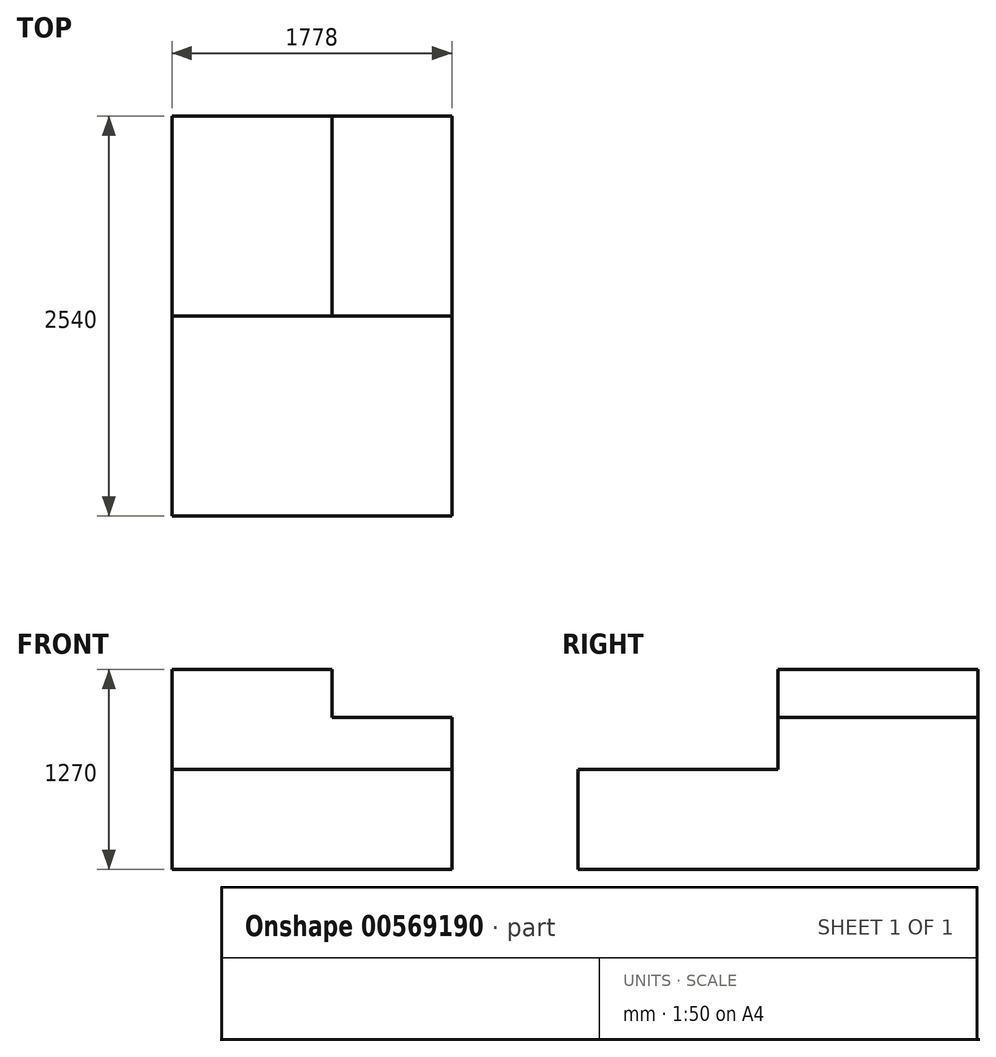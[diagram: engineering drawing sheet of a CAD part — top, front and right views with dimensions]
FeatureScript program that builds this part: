
annotation { "Feature Type Name" : "Feature", "Feature Type Description" : "" }
export const myFeature = defineFeature(function(context is Context, id is Id, definition is map)
    precondition{}
    {
        {
            var Q0;
            Q0=qCreatedBy(makeId("Front.planeOp"),FACE);
            var sketch = newSketch(context, id + "F0", { "sketchPlane" : qUnion([Q0])});
            skLineSegment(sketch, "E0", {"start": v(-77.02, -75.37) * mm, "end": v(1700.98, -75.37) * mm});
            skLineSegment(sketch, "E1", {"start": v(1700.98, -75.37) * mm, "end": v(1700.98, 889.83) * mm});
            skLineSegment(sketch, "E2", {"start": v(-77.02, -75.37) * mm, "end": v(-77.02, 559.63) * mm});
            skLineSegment(sketch, "E3", {"start": v(-77.02, 559.63) * mm, "end": v(1700.98, 559.63) * mm});
            skLineSegment(sketch, "E4", {"start": v(1700.98, 889.83) * mm, "end": v(938.98, 889.83) * mm});
            skLineSegment(sketch, "E5", {"start": v(938.98, 889.83) * mm, "end": v(938.98, 1194.63) * mm});
            skLineSegment(sketch, "E6", {"start": v(938.98, 1194.63) * mm, "end": v(-77.02, 1194.63) * mm});
            skLineSegment(sketch, "E7", {"start": v(-77.02, 1194.63) * mm, "end": v(-77.02, 559.63) * mm});
            skSolve(sketch);
        }
        {
            var Q0;
            {var subQ0=sQuery(id+"F0.wireOp",EDGE,"E0");Q0=makeQuery(id+"F0.imprint","IMPRINT",FACE,{"disambiguationData":[TD([[makeQuery(id+"F0.imprint","IMPRINT",EDGE,{"derivedFrom":subQ0}),1.0]])]});}
            var Q1;
            {var subQ1=sQuery(id+"F0.wireOp",EDGE,"E3");Q1=makeQuery(id+"F0.imprint","IMPRINT",FACE,{"disambiguationData":[TD([[makeQuery(id+"F0.imprint","IMPRINT",EDGE,{"derivedFrom":subQ1}),1.0]])]});}
            extrude(context, id + "F1", {"entities" : qUnion([Q0, Q1]), "oppositeDirection" : true, "depth" : 2540 * mm, "offsetDistance" : 25.4 * mm});
        }
        {
            var Q0;
            {var subQ1=sQuery(id+"F0.wireOp",EDGE,"E3");Q0=makeQuery(id+"F0.imprint","IMPRINT",FACE,{"disambiguationData":[TD([[makeQuery(id+"F0.imprint","IMPRINT",EDGE,{"derivedFrom":subQ1}),1.0]])]});}
            extrude(context, id + "F2", {"entities" : qUnion([Q0]), "operationType" : NewBodyOperationType.REMOVE, "oppositeDirection" : true, "depth" : 1270 * mm, "offsetDistance" : 25.4 * mm});
        }
    });
